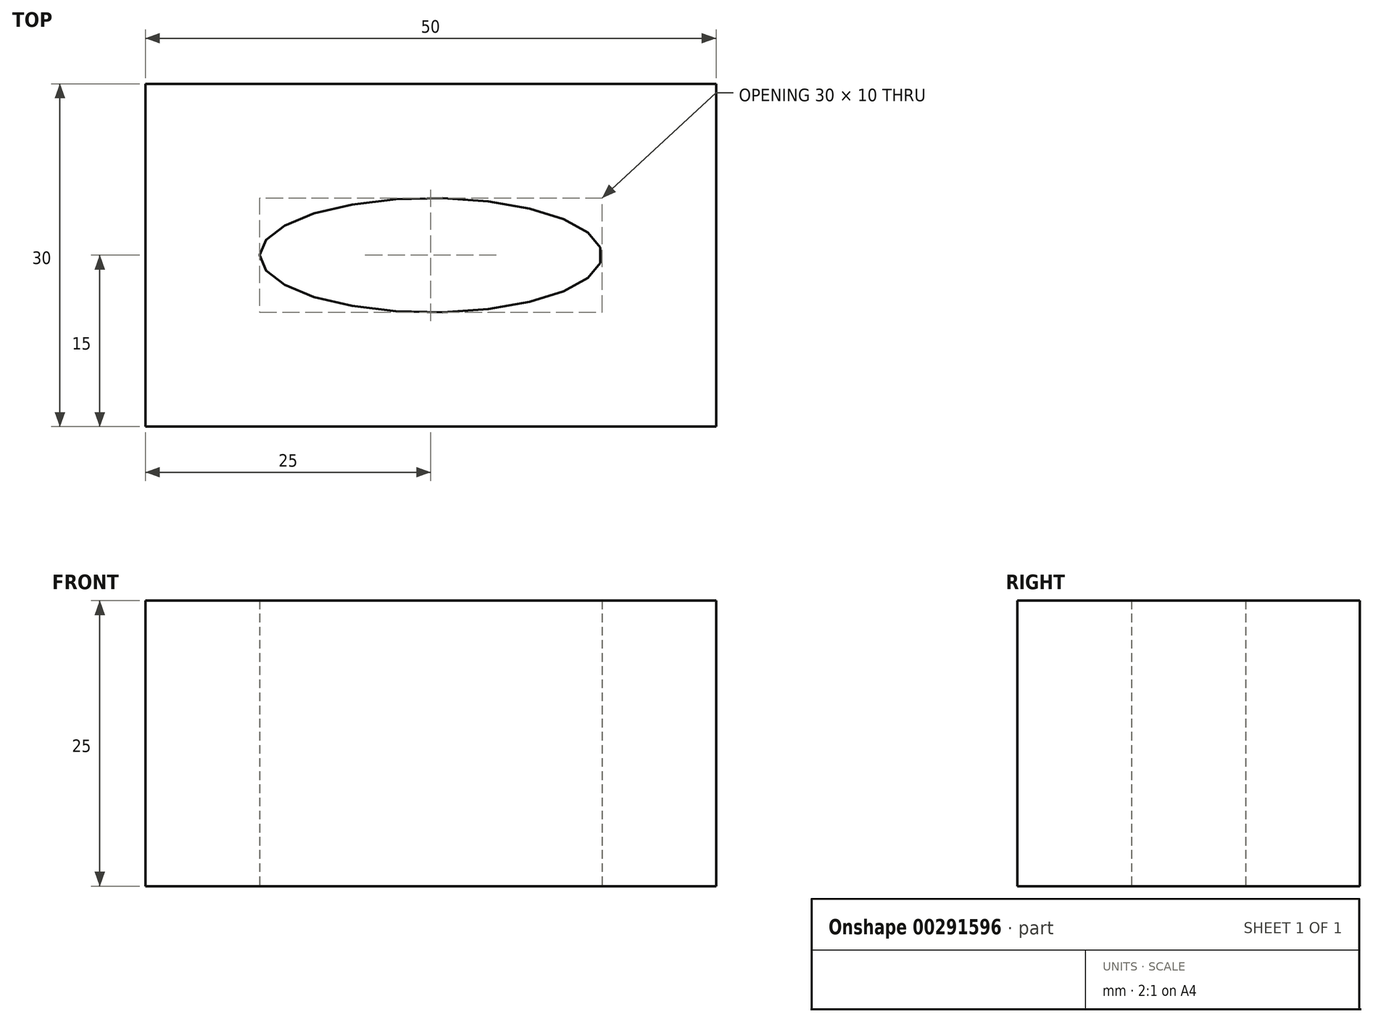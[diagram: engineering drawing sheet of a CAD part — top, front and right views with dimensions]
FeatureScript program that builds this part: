
annotation { "Feature Type Name" : "Feature", "Feature Type Description" : "" }
export const myFeature = defineFeature(function(context is Context, id is Id, definition is map)
    precondition{}
    {
        {
            var Q0;
            Q0=qCreatedBy(makeId("Top.planeOp"),FACE);
            var sketch = newSketch(context, id + "F0", { "sketchPlane" : qUnion([Q0])});
            skLineSegment(sketch, "E0.bottom", {"start": v(25, -15) * mm, "end": v(-25, -15) * mm});
            skLineSegment(sketch, "E0.top", {"start": v(25, 15) * mm, "end": v(-25, 15) * mm});
            skLineSegment(sketch, "E0.left", {"start": v(25, -15) * mm, "end": v(25, 15) * mm});
            skLineSegment(sketch, "E0.right", {"start": v(-25, -15) * mm, "end": v(-25, 15) * mm});
            skPoint(sketch, "E0.middle", {"position": v(0, 0) * mm});
            skEllipse(sketch, "E1", {"center": v(0, 0) * mm, "majorRadius": 15 * mm, "minorRadius": 5 * mm, "majorAxis": v(-1, 0)});
            skSolve(sketch);
        }
        {
            var Q0;
            Q0=makeQuery(id+"F0.imprint","IMPRINT",FACE,{"disambiguationData":[TD([[makeQuery(id+"F0.imprint","IMPRINT",EDGE,{"derivedFrom":sQuery(id+"F0.wireOp",EDGE,"E0.bottom")}),-1.0]])]});
            extrude(context, id + "F1", {"entities" : qUnion([Q0]), "depth" : 25 * mm});
        }
    });
